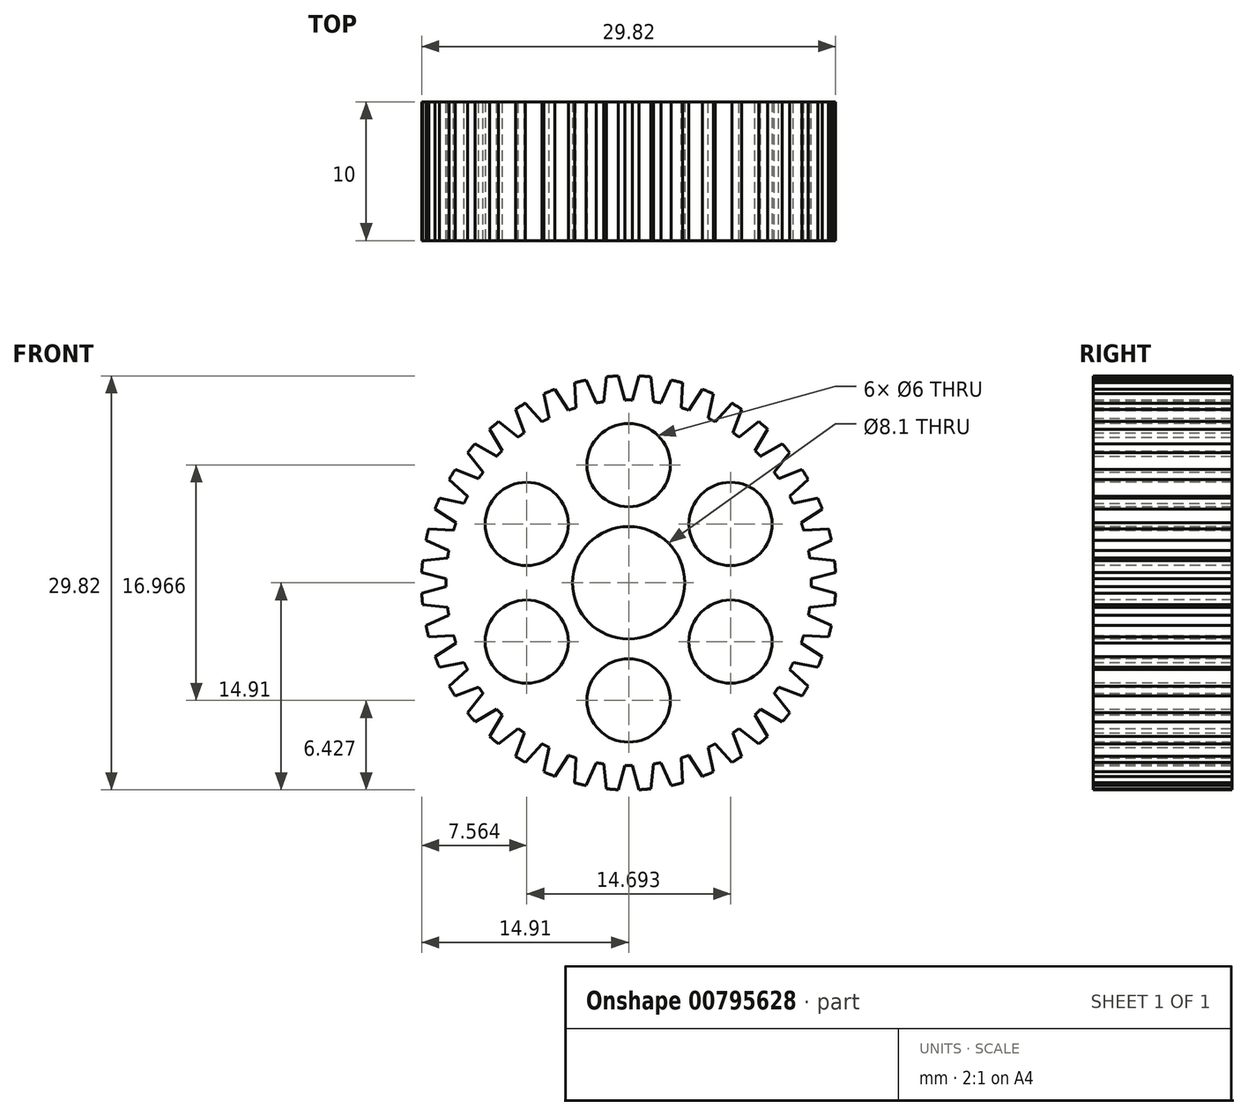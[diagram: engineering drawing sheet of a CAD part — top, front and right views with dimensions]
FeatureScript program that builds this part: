
annotation { "Feature Type Name" : "Feature", "Feature Type Description" : "" }
export const myFeature = defineFeature(function(context is Context, id is Id, definition is map)
    precondition{}
    {
        {
            var Q0;
            Q0=qCreatedBy(makeId("Front.planeOp"),FACE);
            var sketch = newSketch(context, id + "F0", { "sketchPlane" : qUnion([Q0])});
            skLineSegment(sketch, "E0", {"start": v(0, 1.66) * mm, "end": v(0, 25.65) * mm, "construction": true});
            skLineSegment(sketch, "E1", {"start": v(0.28, 20) * mm, "end": v(0.75, 21.74) * mm});
            skLineSegment(sketch, "E2.MirrorCS", {"start": v(-0.28, 20) * mm, "end": v(-0.75, 21.74) * mm});
            skLineSegment(sketch, "E3", {"start": v(-0.28, 20) * mm, "end": v(0, 18.94) * mm, "construction": true});
            skLineSegment(sketch, "E4", {"start": v(0.28, 20) * mm, "end": v(0, 18.94) * mm, "construction": true});
            skLineSegment(sketch, "E5.1.0", {"start": v(-1.78, 19.88) * mm, "end": v(-1.6, 21.67) * mm});
            skLineSegment(sketch, "E5.1.1", {"start": v(-2.34, 19.8) * mm, "end": v(-3.07, 21.44) * mm});
            skLineSegment(sketch, "E5.2.0", {"start": v(-3.8, 19.44) * mm, "end": v(-3.9, 21.24) * mm});
            skLineSegment(sketch, "E5.2.1", {"start": v(-4.34, 19.27) * mm, "end": v(-5.32, 20.78) * mm});
            skLineSegment(sketch, "E5.3.0", {"start": v(-5.73, 18.7) * mm, "end": v(-6.1, 20.45) * mm});
            skLineSegment(sketch, "E5.3.1", {"start": v(-6.23, 18.43) * mm, "end": v(-7.44, 19.77) * mm});
            skLineSegment(sketch, "E5.4.0", {"start": v(-7.51, 17.65) * mm, "end": v(-8.16, 19.33) * mm});
            skLineSegment(sketch, "E5.4.1", {"start": v(-7.97, 17.32) * mm, "end": v(-9.37, 18.45) * mm});
            skLineSegment(sketch, "E5.5.0", {"start": v(-9.11, 16.34) * mm, "end": v(-10.01, 17.9) * mm});
            skLineSegment(sketch, "E5.5.1", {"start": v(-9.51, 15.94) * mm, "end": v(-11.07, 16.84) * mm});
            skLineSegment(sketch, "E5.6.0", {"start": v(-10.49, 14.8) * mm, "end": v(-11.62, 16.2) * mm});
            skLineSegment(sketch, "E5.6.1", {"start": v(-10.82, 14.34) * mm, "end": v(-12.5, 14.99) * mm});
            skLineSegment(sketch, "E5.7.0", {"start": v(-11.6, 13.06) * mm, "end": v(-12.94, 14.27) * mm});
            skLineSegment(sketch, "E5.7.1", {"start": v(-11.86, 12.56) * mm, "end": v(-13.62, 12.93) * mm});
            skLineSegment(sketch, "E5.8.0", {"start": v(-12.44, 11.17) * mm, "end": v(-13.95, 12.15) * mm});
            skLineSegment(sketch, "E5.8.1", {"start": v(-12.61, 10.63) * mm, "end": v(-14.4, 10.72) * mm});
            skLineSegment(sketch, "E5.9.0", {"start": v(-12.96, 9.17) * mm, "end": v(-14.6, 9.9) * mm});
            skLineSegment(sketch, "E5.9.1", {"start": v(-13.05, 8.6) * mm, "end": v(-14.84, 8.42) * mm});
            skLineSegment(sketch, "E5.10.0", {"start": v(-13.17, 7.11) * mm, "end": v(-14.9, 7.58) * mm});
            skLineSegment(sketch, "E5.10.1", {"start": v(-13.17, 6.55) * mm, "end": v(-14.9, 6.08) * mm});
            skLineSegment(sketch, "E5.11.0", {"start": v(-13.05, 5.05) * mm, "end": v(-14.84, 5.24) * mm});
            skLineSegment(sketch, "E5.11.1", {"start": v(-12.96, 4.49) * mm, "end": v(-14.6, 3.76) * mm});
            skLineSegment(sketch, "E5.12.0", {"start": v(-12.61, 3.03) * mm, "end": v(-14.4, 2.94) * mm});
            skLineSegment(sketch, "E5.12.1", {"start": v(-12.44, 2.5) * mm, "end": v(-13.95, 1.51) * mm});
            skLineSegment(sketch, "E5.13.0", {"start": v(-11.86, 1.1) * mm, "end": v(-13.62, 0.73) * mm});
            skLineSegment(sketch, "E5.13.1", {"start": v(-11.6, 0.6) * mm, "end": v(-12.94, -0.6) * mm});
            skLineSegment(sketch, "E5.14.0", {"start": v(-10.82, -0.68) * mm, "end": v(-12.5, -1.33) * mm});
            skLineSegment(sketch, "E5.14.1", {"start": v(-10.49, -1.14) * mm, "end": v(-11.62, -2.54) * mm});
            skLineSegment(sketch, "E5.15.0", {"start": v(-9.51, -2.28) * mm, "end": v(-11.07, -3.18) * mm});
            skLineSegment(sketch, "E5.15.1", {"start": v(-9.11, -2.68) * mm, "end": v(-10.01, -4.24) * mm});
            skLineSegment(sketch, "E5.16.0", {"start": v(-7.97, -3.66) * mm, "end": v(-9.37, -4.79) * mm});
            skLineSegment(sketch, "E5.16.1", {"start": v(-7.51, -3.99) * mm, "end": v(-8.16, -5.67) * mm});
            skLineSegment(sketch, "E5.17.0", {"start": v(-6.23, -4.77) * mm, "end": v(-7.44, -6.11) * mm});
            skLineSegment(sketch, "E5.17.1", {"start": v(-5.73, -5.03) * mm, "end": v(-6.1, -6.8) * mm});
            skLineSegment(sketch, "E5.18.0", {"start": v(-4.34, -5.6) * mm, "end": v(-5.32, -7.12) * mm});
            skLineSegment(sketch, "E5.18.1", {"start": v(-3.8, -5.78) * mm, "end": v(-3.9, -7.58) * mm});
            skLineSegment(sketch, "E5.19.0", {"start": v(-2.34, -6.13) * mm, "end": v(-3.07, -7.78) * mm});
            skLineSegment(sketch, "E5.19.1", {"start": v(-1.78, -6.22) * mm, "end": v(-1.6, -8.01) * mm});
            skLineSegment(sketch, "E5.20.0", {"start": v(-0.28, -6.34) * mm, "end": v(-0.75, -8.08) * mm});
            skLineSegment(sketch, "E5.20.1", {"start": v(0.28, -6.34) * mm, "end": v(0.75, -8.08) * mm});
            skLineSegment(sketch, "E5.21.0", {"start": v(1.78, -6.22) * mm, "end": v(1.6, -8.01) * mm});
            skLineSegment(sketch, "E5.21.1", {"start": v(2.34, -6.13) * mm, "end": v(3.07, -7.78) * mm});
            skLineSegment(sketch, "E5.22.0", {"start": v(3.8, -5.78) * mm, "end": v(3.9, -7.58) * mm});
            skLineSegment(sketch, "E5.22.1", {"start": v(4.34, -5.6) * mm, "end": v(5.32, -7.12) * mm});
            skLineSegment(sketch, "E5.23.0", {"start": v(5.73, -5.03) * mm, "end": v(6.1, -6.8) * mm});
            skLineSegment(sketch, "E5.23.1", {"start": v(6.23, -4.77) * mm, "end": v(7.44, -6.11) * mm});
            skLineSegment(sketch, "E5.24.0", {"start": v(7.51, -3.99) * mm, "end": v(8.16, -5.67) * mm});
            skLineSegment(sketch, "E5.24.1", {"start": v(7.97, -3.66) * mm, "end": v(9.37, -4.79) * mm});
            skLineSegment(sketch, "E5.25.0", {"start": v(9.11, -2.68) * mm, "end": v(10.01, -4.24) * mm});
            skLineSegment(sketch, "E5.25.1", {"start": v(9.51, -2.28) * mm, "end": v(11.07, -3.18) * mm});
            skLineSegment(sketch, "E5.26.0", {"start": v(10.49, -1.14) * mm, "end": v(11.62, -2.54) * mm});
            skLineSegment(sketch, "E5.26.1", {"start": v(10.82, -0.68) * mm, "end": v(12.5, -1.33) * mm});
            skLineSegment(sketch, "E5.27.0", {"start": v(11.6, 0.6) * mm, "end": v(12.94, -0.6) * mm});
            skLineSegment(sketch, "E5.27.1", {"start": v(11.86, 1.1) * mm, "end": v(13.62, 0.73) * mm});
            skLineSegment(sketch, "E5.28.0", {"start": v(12.44, 2.5) * mm, "end": v(13.95, 1.51) * mm});
            skLineSegment(sketch, "E5.28.1", {"start": v(12.61, 3.03) * mm, "end": v(14.4, 2.94) * mm});
            skLineSegment(sketch, "E5.29.0", {"start": v(12.96, 4.49) * mm, "end": v(14.6, 3.76) * mm});
            skLineSegment(sketch, "E5.29.1", {"start": v(13.05, 5.05) * mm, "end": v(14.84, 5.24) * mm});
            skLineSegment(sketch, "E5.30.0", {"start": v(13.17, 6.55) * mm, "end": v(14.9, 6.08) * mm});
            skLineSegment(sketch, "E5.30.1", {"start": v(13.17, 7.11) * mm, "end": v(14.9, 7.58) * mm});
            skLineSegment(sketch, "E5.31.0", {"start": v(13.05, 8.6) * mm, "end": v(14.84, 8.42) * mm});
            skLineSegment(sketch, "E5.31.1", {"start": v(12.96, 9.17) * mm, "end": v(14.6, 9.9) * mm});
            skLineSegment(sketch, "E5.32.0", {"start": v(12.61, 10.63) * mm, "end": v(14.4, 10.72) * mm});
            skLineSegment(sketch, "E5.32.1", {"start": v(12.44, 11.17) * mm, "end": v(13.95, 12.15) * mm});
            skLineSegment(sketch, "E5.33.0", {"start": v(11.86, 12.56) * mm, "end": v(13.62, 12.93) * mm});
            skLineSegment(sketch, "E5.33.1", {"start": v(11.6, 13.06) * mm, "end": v(12.94, 14.27) * mm});
            skLineSegment(sketch, "E5.34.0", {"start": v(10.82, 14.34) * mm, "end": v(12.5, 14.99) * mm});
            skLineSegment(sketch, "E5.34.1", {"start": v(10.49, 14.8) * mm, "end": v(11.62, 16.2) * mm});
            skLineSegment(sketch, "E5.35.0", {"start": v(9.51, 15.94) * mm, "end": v(11.07, 16.84) * mm});
            skLineSegment(sketch, "E5.35.1", {"start": v(9.11, 16.34) * mm, "end": v(10.01, 17.9) * mm});
            skLineSegment(sketch, "E5.36.0", {"start": v(7.97, 17.32) * mm, "end": v(9.37, 18.45) * mm});
            skLineSegment(sketch, "E5.36.1", {"start": v(7.51, 17.65) * mm, "end": v(8.16, 19.33) * mm});
            skLineSegment(sketch, "E5.37.0", {"start": v(6.23, 18.43) * mm, "end": v(7.44, 19.77) * mm});
            skLineSegment(sketch, "E5.37.1", {"start": v(5.73, 18.7) * mm, "end": v(6.1, 20.45) * mm});
            skLineSegment(sketch, "E5.38.0", {"start": v(4.34, 19.27) * mm, "end": v(5.32, 20.78) * mm});
            skLineSegment(sketch, "E5.38.1", {"start": v(3.8, 19.44) * mm, "end": v(3.9, 21.24) * mm});
            skLineSegment(sketch, "E5.39.0", {"start": v(2.34, 19.8) * mm, "end": v(3.07, 21.44) * mm});
            skLineSegment(sketch, "E5.39.1", {"start": v(1.78, 19.88) * mm, "end": v(1.6, 21.67) * mm});
            skPoint(sketch, "E5.center", {"position": v(0, 6.83) * mm});
            skArc(sketch, "E6", {"start": v(0.28, 20) * mm, "mid": v(0, 20) * mm, "end": v(-0.28, 20) * mm});
            skArc(sketch, "E7", {"start": v(-0.75, 21.74) * mm, "mid": v(-1.17, 21.7) * mm, "end": v(-1.6, 21.67) * mm});
            skArc(sketch, "E8.trimOffspring", {"start": v(1.6, 21.67) * mm, "mid": v(1.17, 21.7) * mm, "end": v(0.75, 21.74) * mm});
            skArc(sketch, "E9.trimOffspring", {"start": v(2.34, 19.8) * mm, "mid": v(2.06, 19.84) * mm, "end": v(1.78, 19.88) * mm});
            skArc(sketch, "E10.trimOffspring", {"start": v(3.9, 21.24) * mm, "mid": v(3.48, 21.34) * mm, "end": v(3.07, 21.44) * mm});
            skArc(sketch, "E11.trimOffspring", {"start": v(4.34, 19.27) * mm, "mid": v(4.07, 19.36) * mm, "end": v(3.8, 19.44) * mm});
            skArc(sketch, "E12.trimOffspring", {"start": v(6.1, 20.45) * mm, "mid": v(5.71, 20.62) * mm, "end": v(5.32, 20.78) * mm});
            skArc(sketch, "E13.trimOffspring", {"start": v(6.23, 18.43) * mm, "mid": v(5.98, 18.57) * mm, "end": v(5.73, 18.7) * mm});
            skArc(sketch, "E14.trimOffspring", {"start": v(8.16, 19.33) * mm, "mid": v(7.8, 19.56) * mm, "end": v(7.44, 19.77) * mm});
            skArc(sketch, "E15.trimOffspring", {"start": v(7.97, 17.32) * mm, "mid": v(7.74, 17.49) * mm, "end": v(7.51, 17.65) * mm});
            skArc(sketch, "E16.trimOffspring", {"start": v(10.01, 17.9) * mm, "mid": v(9.7, 18.18) * mm, "end": v(9.37, 18.45) * mm});
            skArc(sketch, "E17.trimOffspring", {"start": v(9.51, 15.94) * mm, "mid": v(9.31, 16.14) * mm, "end": v(9.11, 16.34) * mm});
            skArc(sketch, "E18.trimOffspring", {"start": v(11.62, 16.2) * mm, "mid": v(11.35, 16.52) * mm, "end": v(11.07, 16.84) * mm});
            skArc(sketch, "E19.trimOffspring", {"start": v(10.82, 14.34) * mm, "mid": v(10.66, 14.57) * mm, "end": v(10.49, 14.8) * mm});
            skArc(sketch, "E20.trimOffspring", {"start": v(12.94, 14.27) * mm, "mid": v(12.73, 14.63) * mm, "end": v(12.5, 14.99) * mm});
            skArc(sketch, "E21.trimOffspring", {"start": v(11.86, 12.56) * mm, "mid": v(11.74, 12.8) * mm, "end": v(11.6, 13.06) * mm});
            skArc(sketch, "E22.trimOffspring", {"start": v(13.95, 12.15) * mm, "mid": v(13.79, 12.54) * mm, "end": v(13.62, 12.93) * mm});
            skArc(sketch, "E23.trimOffspring", {"start": v(12.61, 10.63) * mm, "mid": v(12.53, 10.9) * mm, "end": v(12.44, 11.17) * mm});
            skArc(sketch, "E24.trimOffspring", {"start": v(14.6, 9.9) * mm, "mid": v(14.51, 10.31) * mm, "end": v(14.4, 10.72) * mm});
            skArc(sketch, "E25.trimOffspring", {"start": v(13.05, 8.6) * mm, "mid": v(13, 8.9) * mm, "end": v(12.96, 9.17) * mm});
            skArc(sketch, "E26.trimOffspring", {"start": v(14.9, 7.58) * mm, "mid": v(14.88, 8) * mm, "end": v(14.84, 8.42) * mm});
            skArc(sketch, "E27.trimOffspring", {"start": v(14.84, 5.24) * mm, "mid": v(14.88, 5.66) * mm, "end": v(14.9, 6.08) * mm});
            skArc(sketch, "E28.trimOffspring", {"start": v(14.4, 2.94) * mm, "mid": v(14.51, 3.35) * mm, "end": v(14.6, 3.76) * mm});
            skArc(sketch, "E29.trimOffspring", {"start": v(13.62, 0.73) * mm, "mid": v(13.79, 1.12) * mm, "end": v(13.95, 1.51) * mm});
            skArc(sketch, "E30.trimOffspring", {"start": v(12.5, -1.33) * mm, "mid": v(12.73, -0.97) * mm, "end": v(12.94, -0.6) * mm});
            skArc(sketch, "E31.trimOffspring", {"start": v(11.07, -3.18) * mm, "mid": v(11.35, -2.86) * mm, "end": v(11.62, -2.54) * mm});
            skArc(sketch, "E32.trimOffspring", {"start": v(13.17, 6.55) * mm, "mid": v(13.17, 6.83) * mm, "end": v(13.17, 7.11) * mm});
            skArc(sketch, "E33.trimOffspring", {"start": v(12.96, 4.49) * mm, "mid": v(13, 4.77) * mm, "end": v(13.05, 5.05) * mm});
            skArc(sketch, "E34.trimOffspring", {"start": v(12.44, 2.5) * mm, "mid": v(12.53, 2.76) * mm, "end": v(12.61, 3.03) * mm});
            skArc(sketch, "E35.trimOffspring", {"start": v(11.6, 0.6) * mm, "mid": v(11.74, 0.85) * mm, "end": v(11.86, 1.1) * mm});
            skArc(sketch, "E36.trimOffspring", {"start": v(10.49, -1.14) * mm, "mid": v(10.66, -0.91) * mm, "end": v(10.82, -0.68) * mm});
            skArc(sketch, "E37.trimOffspring", {"start": v(9.11, -2.68) * mm, "mid": v(9.31, -2.48) * mm, "end": v(9.51, -2.28) * mm});
            skArc(sketch, "E38.trimOffspring", {"start": v(9.37, -4.79) * mm, "mid": v(9.7, -4.52) * mm, "end": v(10.01, -4.24) * mm});
            skArc(sketch, "E39.trimOffspring", {"start": v(7.44, -6.11) * mm, "mid": v(7.8, -5.9) * mm, "end": v(8.16, -5.67) * mm});
            skArc(sketch, "E40.trimOffspring", {"start": v(5.32, -7.12) * mm, "mid": v(5.71, -6.96) * mm, "end": v(6.1, -6.8) * mm});
            skArc(sketch, "E41.trimOffspring", {"start": v(3.07, -7.78) * mm, "mid": v(3.48, -7.68) * mm, "end": v(3.9, -7.58) * mm});
            skArc(sketch, "E42.trimOffspring", {"start": v(0.75, -8.08) * mm, "mid": v(1.17, -8.05) * mm, "end": v(1.6, -8.01) * mm});
            skArc(sketch, "E43.trimOffspring", {"start": v(-1.6, -8.01) * mm, "mid": v(-1.17, -8.05) * mm, "end": v(-0.75, -8.08) * mm});
            skArc(sketch, "E44.trimOffspring", {"start": v(-3.9, -7.58) * mm, "mid": v(-3.48, -7.68) * mm, "end": v(-3.07, -7.78) * mm});
            skArc(sketch, "E45.trimOffspring", {"start": v(-6.1, -6.8) * mm, "mid": v(-5.71, -6.96) * mm, "end": v(-5.32, -7.12) * mm});
            skArc(sketch, "E46.trimOffspring", {"start": v(-8.16, -5.67) * mm, "mid": v(-7.8, -5.9) * mm, "end": v(-7.44, -6.11) * mm});
            skArc(sketch, "E47.trimOffspring", {"start": v(-6.23, -4.77) * mm, "mid": v(-5.98, -4.9) * mm, "end": v(-5.73, -5.03) * mm});
            skArc(sketch, "E48.trimOffspring", {"start": v(-4.34, -5.6) * mm, "mid": v(-4.07, -5.7) * mm, "end": v(-3.8, -5.78) * mm});
            skArc(sketch, "E49.trimOffspring", {"start": v(-2.34, -6.13) * mm, "mid": v(-2.06, -6.18) * mm, "end": v(-1.78, -6.22) * mm});
            skArc(sketch, "E50.trimOffspring", {"start": v(-0.28, -6.34) * mm, "mid": v(0, -6.34) * mm, "end": v(0.28, -6.34) * mm});
            skArc(sketch, "E51.trimOffspring", {"start": v(1.78, -6.22) * mm, "mid": v(2.06, -6.18) * mm, "end": v(2.34, -6.13) * mm});
            skArc(sketch, "E52.trimOffspring", {"start": v(3.8, -5.78) * mm, "mid": v(4.07, -5.7) * mm, "end": v(4.34, -5.6) * mm});
            skArc(sketch, "E53.trimOffspring", {"start": v(5.73, -5.03) * mm, "mid": v(5.98, -4.9) * mm, "end": v(6.23, -4.77) * mm});
            skArc(sketch, "E54.trimOffspring", {"start": v(7.51, -3.99) * mm, "mid": v(7.74, -3.83) * mm, "end": v(7.97, -3.66) * mm});
            skArc(sketch, "E55.trimOffspring", {"start": v(-10.01, -4.24) * mm, "mid": v(-9.7, -4.52) * mm, "end": v(-9.37, -4.79) * mm});
            skArc(sketch, "E56.trimOffspring", {"start": v(-11.62, -2.54) * mm, "mid": v(-11.35, -2.86) * mm, "end": v(-11.07, -3.18) * mm});
            skArc(sketch, "E57.trimOffspring", {"start": v(-12.94, -0.6) * mm, "mid": v(-12.73, -0.97) * mm, "end": v(-12.5, -1.33) * mm});
            skArc(sketch, "E58.trimOffspring", {"start": v(-13.95, 1.51) * mm, "mid": v(-13.79, 1.12) * mm, "end": v(-13.62, 0.73) * mm});
            skArc(sketch, "E59.trimOffspring", {"start": v(-11.86, 1.1) * mm, "mid": v(-11.74, 0.85) * mm, "end": v(-11.6, 0.6) * mm});
            skArc(sketch, "E60.trimOffspring", {"start": v(-10.82, -0.68) * mm, "mid": v(-10.66, -0.91) * mm, "end": v(-10.49, -1.14) * mm});
            skArc(sketch, "E61.trimOffspring", {"start": v(-9.51, -2.28) * mm, "mid": v(-9.31, -2.48) * mm, "end": v(-9.11, -2.68) * mm});
            skArc(sketch, "E62.trimOffspring", {"start": v(-7.97, -3.66) * mm, "mid": v(-7.74, -3.83) * mm, "end": v(-7.51, -3.99) * mm});
            skArc(sketch, "E63.trimOffspring", {"start": v(-14.6, 3.76) * mm, "mid": v(-14.51, 3.35) * mm, "end": v(-14.4, 2.94) * mm});
            skArc(sketch, "E64.trimOffspring", {"start": v(-14.9, 6.08) * mm, "mid": v(-14.88, 5.66) * mm, "end": v(-14.84, 5.24) * mm});
            skArc(sketch, "E65.trimOffspring", {"start": v(-14.84, 8.42) * mm, "mid": v(-14.88, 8) * mm, "end": v(-14.9, 7.58) * mm});
            skArc(sketch, "E66.trimOffspring", {"start": v(-14.4, 10.72) * mm, "mid": v(-14.51, 10.31) * mm, "end": v(-14.6, 9.9) * mm});
            skArc(sketch, "E67.trimOffspring", {"start": v(-13.62, 12.93) * mm, "mid": v(-13.79, 12.54) * mm, "end": v(-13.95, 12.15) * mm});
            skArc(sketch, "E68.trimOffspring", {"start": v(-12.5, 14.99) * mm, "mid": v(-12.73, 14.63) * mm, "end": v(-12.94, 14.27) * mm});
            skArc(sketch, "E69.trimOffspring", {"start": v(-11.07, 16.84) * mm, "mid": v(-11.35, 16.52) * mm, "end": v(-11.62, 16.2) * mm});
            skArc(sketch, "E70.trimOffspring", {"start": v(-9.37, 18.45) * mm, "mid": v(-9.7, 18.18) * mm, "end": v(-10.01, 17.9) * mm});
            skArc(sketch, "E71.trimOffspring", {"start": v(-7.44, 19.77) * mm, "mid": v(-7.8, 19.56) * mm, "end": v(-8.16, 19.33) * mm});
            skArc(sketch, "E72.trimOffspring", {"start": v(-5.32, 20.78) * mm, "mid": v(-5.71, 20.62) * mm, "end": v(-6.1, 20.45) * mm});
            skArc(sketch, "E73.trimOffspring", {"start": v(-3.07, 21.44) * mm, "mid": v(-3.48, 21.34) * mm, "end": v(-3.9, 21.24) * mm});
            skArc(sketch, "E74.trimOffspring", {"start": v(-1.78, 19.88) * mm, "mid": v(-2.06, 19.84) * mm, "end": v(-2.34, 19.8) * mm});
            skArc(sketch, "E75.trimOffspring", {"start": v(-3.8, 19.44) * mm, "mid": v(-4.07, 19.36) * mm, "end": v(-4.34, 19.27) * mm});
            skArc(sketch, "E76.trimOffspring", {"start": v(-5.73, 18.7) * mm, "mid": v(-5.98, 18.57) * mm, "end": v(-6.23, 18.43) * mm});
            skArc(sketch, "E77.trimOffspring", {"start": v(-7.51, 17.65) * mm, "mid": v(-7.74, 17.49) * mm, "end": v(-7.97, 17.32) * mm});
            skArc(sketch, "E78.trimOffspring", {"start": v(-9.11, 16.34) * mm, "mid": v(-9.31, 16.14) * mm, "end": v(-9.51, 15.94) * mm});
            skArc(sketch, "E79.trimOffspring", {"start": v(-10.49, 14.8) * mm, "mid": v(-10.66, 14.57) * mm, "end": v(-10.82, 14.34) * mm});
            skArc(sketch, "E80.trimOffspring", {"start": v(-11.6, 13.06) * mm, "mid": v(-11.74, 12.8) * mm, "end": v(-11.86, 12.56) * mm});
            skArc(sketch, "E81.trimOffspring", {"start": v(-12.44, 11.17) * mm, "mid": v(-12.53, 10.9) * mm, "end": v(-12.61, 10.63) * mm});
            skArc(sketch, "E82.trimOffspring", {"start": v(-12.96, 9.17) * mm, "mid": v(-13, 8.9) * mm, "end": v(-13.05, 8.6) * mm});
            skArc(sketch, "E83.trimOffspring", {"start": v(-13.17, 7.11) * mm, "mid": v(-13.17, 6.83) * mm, "end": v(-13.17, 6.55) * mm});
            skArc(sketch, "E84.trimOffspring", {"start": v(-13.05, 5.05) * mm, "mid": v(-13, 4.77) * mm, "end": v(-12.96, 4.49) * mm});
            skArc(sketch, "E85.trimOffspring", {"start": v(-12.61, 3.03) * mm, "mid": v(-12.53, 2.76) * mm, "end": v(-12.44, 2.5) * mm});
            skSolve(sketch);
        }
        {
            var Q0;
            Q0 = qSketchRegion(id + "F0", true);
            extrude(context, id + "F1", {"entities" : qUnion([Q0]), "depth" : 10 * mm, "offsetDistance" : 25 * mm});
        }
        {
            var Q0;
            Q0=makeQuery(id+"F1.opExtrude","CAP_FACE",FACE,{"disambiguationData":[OSD([sQuery(id+"F0.wireOp",EDGE,"E1"),sQuery(id+"F0.wireOp",EDGE,"E2.MirrorCS"),sQuery(id+"F0.wireOp",EDGE,"E5.1.0"),sQuery(id+"F0.wireOp",EDGE,"E5.1.1"),sQuery(id+"F0.wireOp",EDGE,"E5.2.0"),sQuery(id+"F0.wireOp",EDGE,"E5.2.1"),sQuery(id+"F0.wireOp",EDGE,"E5.3.0"),sQuery(id+"F0.wireOp",EDGE,"E5.3.1"),sQuery(id+"F0.wireOp",EDGE,"E5.4.0"),sQuery(id+"F0.wireOp",EDGE,"E5.4.1"),sQuery(id+"F0.wireOp",EDGE,"E5.5.0"),sQuery(id+"F0.wireOp",EDGE,"E5.5.1"),sQuery(id+"F0.wireOp",EDGE,"E5.6.0"),sQuery(id+"F0.wireOp",EDGE,"E5.6.1"),sQuery(id+"F0.wireOp",EDGE,"E5.7.0"),sQuery(id+"F0.wireOp",EDGE,"E5.7.1"),sQuery(id+"F0.wireOp",EDGE,"E5.8.0"),sQuery(id+"F0.wireOp",EDGE,"E5.8.1"),sQuery(id+"F0.wireOp",EDGE,"E5.9.0"),sQuery(id+"F0.wireOp",EDGE,"E5.9.1"),sQuery(id+"F0.wireOp",EDGE,"E5.10.0"),sQuery(id+"F0.wireOp",EDGE,"E5.10.1"),sQuery(id+"F0.wireOp",EDGE,"E5.11.0"),sQuery(id+"F0.wireOp",EDGE,"E5.11.1"),sQuery(id+"F0.wireOp",EDGE,"E5.12.0"),sQuery(id+"F0.wireOp",EDGE,"E5.12.1"),sQuery(id+"F0.wireOp",EDGE,"E5.13.0"),sQuery(id+"F0.wireOp",EDGE,"E5.13.1"),sQuery(id+"F0.wireOp",EDGE,"E5.14.0"),sQuery(id+"F0.wireOp",EDGE,"E5.14.1"),sQuery(id+"F0.wireOp",EDGE,"E5.15.0"),sQuery(id+"F0.wireOp",EDGE,"E5.15.1"),sQuery(id+"F0.wireOp",EDGE,"E5.16.0"),sQuery(id+"F0.wireOp",EDGE,"E5.16.1"),sQuery(id+"F0.wireOp",EDGE,"E5.17.0"),sQuery(id+"F0.wireOp",EDGE,"E5.17.1"),sQuery(id+"F0.wireOp",EDGE,"E5.18.0"),sQuery(id+"F0.wireOp",EDGE,"E5.18.1"),sQuery(id+"F0.wireOp",EDGE,"E5.19.0"),sQuery(id+"F0.wireOp",EDGE,"E5.19.1"),sQuery(id+"F0.wireOp",EDGE,"E5.20.0"),sQuery(id+"F0.wireOp",EDGE,"E5.20.1"),sQuery(id+"F0.wireOp",EDGE,"E5.21.0"),sQuery(id+"F0.wireOp",EDGE,"E5.21.1"),sQuery(id+"F0.wireOp",EDGE,"E5.22.0"),sQuery(id+"F0.wireOp",EDGE,"E5.22.1"),sQuery(id+"F0.wireOp",EDGE,"E5.23.0"),sQuery(id+"F0.wireOp",EDGE,"E5.23.1"),sQuery(id+"F0.wireOp",EDGE,"E5.24.0"),sQuery(id+"F0.wireOp",EDGE,"E5.24.1"),sQuery(id+"F0.wireOp",EDGE,"E5.25.0"),sQuery(id+"F0.wireOp",EDGE,"E5.25.1"),sQuery(id+"F0.wireOp",EDGE,"E5.26.0"),sQuery(id+"F0.wireOp",EDGE,"E5.26.1"),sQuery(id+"F0.wireOp",EDGE,"E5.27.0"),sQuery(id+"F0.wireOp",EDGE,"E5.27.1"),sQuery(id+"F0.wireOp",EDGE,"E5.28.0"),sQuery(id+"F0.wireOp",EDGE,"E5.28.1"),sQuery(id+"F0.wireOp",EDGE,"E5.29.0"),sQuery(id+"F0.wireOp",EDGE,"E5.29.1"),sQuery(id+"F0.wireOp",EDGE,"E5.30.0"),sQuery(id+"F0.wireOp",EDGE,"E5.30.1"),sQuery(id+"F0.wireOp",EDGE,"E5.31.0"),sQuery(id+"F0.wireOp",EDGE,"E5.31.1"),sQuery(id+"F0.wireOp",EDGE,"E5.32.0"),sQuery(id+"F0.wireOp",EDGE,"E5.32.1"),sQuery(id+"F0.wireOp",EDGE,"E5.33.0"),sQuery(id+"F0.wireOp",EDGE,"E5.33.1"),sQuery(id+"F0.wireOp",EDGE,"E5.34.0"),sQuery(id+"F0.wireOp",EDGE,"E5.34.1"),sQuery(id+"F0.wireOp",EDGE,"E5.35.0"),sQuery(id+"F0.wireOp",EDGE,"E5.35.1"),sQuery(id+"F0.wireOp",EDGE,"E5.36.0"),sQuery(id+"F0.wireOp",EDGE,"E5.36.1"),sQuery(id+"F0.wireOp",EDGE,"E5.37.0"),sQuery(id+"F0.wireOp",EDGE,"E5.37.1"),sQuery(id+"F0.wireOp",EDGE,"E5.38.0"),sQuery(id+"F0.wireOp",EDGE,"E5.38.1"),sQuery(id+"F0.wireOp",EDGE,"E5.39.0"),sQuery(id+"F0.wireOp",EDGE,"E5.39.1"),sQuery(id+"F0.wireOp",EDGE,"E6"),sQuery(id+"F0.wireOp",EDGE,"E7"),sQuery(id+"F0.wireOp",EDGE,"E8.trimOffspring"),sQuery(id+"F0.wireOp",EDGE,"E9.trimOffspring"),sQuery(id+"F0.wireOp",EDGE,"E10.trimOffspring"),sQuery(id+"F0.wireOp",EDGE,"E11.trimOffspring"),sQuery(id+"F0.wireOp",EDGE,"E12.trimOffspring"),sQuery(id+"F0.wireOp",EDGE,"E13.trimOffspring"),sQuery(id+"F0.wireOp",EDGE,"E14.trimOffspring"),sQuery(id+"F0.wireOp",EDGE,"E15.trimOffspring"),sQuery(id+"F0.wireOp",EDGE,"E16.trimOffspring"),sQuery(id+"F0.wireOp",EDGE,"E17.trimOffspring"),sQuery(id+"F0.wireOp",EDGE,"E18.trimOffspring"),sQuery(id+"F0.wireOp",EDGE,"E19.trimOffspring"),sQuery(id+"F0.wireOp",EDGE,"E20.trimOffspring"),sQuery(id+"F0.wireOp",EDGE,"E21.trimOffspring"),sQuery(id+"F0.wireOp",EDGE,"E22.trimOffspring"),sQuery(id+"F0.wireOp",EDGE,"E23.trimOffspring"),sQuery(id+"F0.wireOp",EDGE,"E24.trimOffspring"),sQuery(id+"F0.wireOp",EDGE,"E25.trimOffspring"),sQuery(id+"F0.wireOp",EDGE,"E26.trimOffspring"),sQuery(id+"F0.wireOp",EDGE,"E27.trimOffspring"),sQuery(id+"F0.wireOp",EDGE,"E28.trimOffspring"),sQuery(id+"F0.wireOp",EDGE,"E29.trimOffspring"),sQuery(id+"F0.wireOp",EDGE,"E30.trimOffspring"),sQuery(id+"F0.wireOp",EDGE,"E31.trimOffspring"),sQuery(id+"F0.wireOp",EDGE,"E32.trimOffspring"),sQuery(id+"F0.wireOp",EDGE,"E33.trimOffspring"),sQuery(id+"F0.wireOp",EDGE,"E34.trimOffspring"),sQuery(id+"F0.wireOp",EDGE,"E35.trimOffspring"),sQuery(id+"F0.wireOp",EDGE,"E36.trimOffspring"),sQuery(id+"F0.wireOp",EDGE,"E37.trimOffspring"),sQuery(id+"F0.wireOp",EDGE,"E38.trimOffspring"),sQuery(id+"F0.wireOp",EDGE,"E39.trimOffspring"),sQuery(id+"F0.wireOp",EDGE,"E40.trimOffspring"),sQuery(id+"F0.wireOp",EDGE,"E41.trimOffspring"),sQuery(id+"F0.wireOp",EDGE,"E42.trimOffspring"),sQuery(id+"F0.wireOp",EDGE,"E43.trimOffspring"),sQuery(id+"F0.wireOp",EDGE,"E44.trimOffspring"),sQuery(id+"F0.wireOp",EDGE,"E45.trimOffspring"),sQuery(id+"F0.wireOp",EDGE,"E46.trimOffspring"),sQuery(id+"F0.wireOp",EDGE,"E47.trimOffspring"),sQuery(id+"F0.wireOp",EDGE,"E48.trimOffspring"),sQuery(id+"F0.wireOp",EDGE,"E49.trimOffspring"),sQuery(id+"F0.wireOp",EDGE,"E50.trimOffspring"),sQuery(id+"F0.wireOp",EDGE,"E51.trimOffspring"),sQuery(id+"F0.wireOp",EDGE,"E52.trimOffspring"),sQuery(id+"F0.wireOp",EDGE,"E53.trimOffspring"),sQuery(id+"F0.wireOp",EDGE,"E54.trimOffspring"),sQuery(id+"F0.wireOp",EDGE,"E55.trimOffspring"),sQuery(id+"F0.wireOp",EDGE,"E56.trimOffspring"),sQuery(id+"F0.wireOp",EDGE,"E57.trimOffspring"),sQuery(id+"F0.wireOp",EDGE,"E58.trimOffspring"),sQuery(id+"F0.wireOp",EDGE,"E59.trimOffspring"),sQuery(id+"F0.wireOp",EDGE,"E60.trimOffspring"),sQuery(id+"F0.wireOp",EDGE,"E61.trimOffspring"),sQuery(id+"F0.wireOp",EDGE,"E62.trimOffspring"),sQuery(id+"F0.wireOp",EDGE,"E63.trimOffspring"),sQuery(id+"F0.wireOp",EDGE,"E64.trimOffspring"),sQuery(id+"F0.wireOp",EDGE,"E65.trimOffspring"),sQuery(id+"F0.wireOp",EDGE,"E66.trimOffspring"),sQuery(id+"F0.wireOp",EDGE,"E67.trimOffspring"),sQuery(id+"F0.wireOp",EDGE,"E68.trimOffspring"),sQuery(id+"F0.wireOp",EDGE,"E69.trimOffspring"),sQuery(id+"F0.wireOp",EDGE,"E70.trimOffspring"),sQuery(id+"F0.wireOp",EDGE,"E71.trimOffspring"),sQuery(id+"F0.wireOp",EDGE,"E72.trimOffspring"),sQuery(id+"F0.wireOp",EDGE,"E73.trimOffspring"),sQuery(id+"F0.wireOp",EDGE,"E74.trimOffspring"),sQuery(id+"F0.wireOp",EDGE,"E75.trimOffspring"),sQuery(id+"F0.wireOp",EDGE,"E76.trimOffspring"),sQuery(id+"F0.wireOp",EDGE,"E77.trimOffspring"),sQuery(id+"F0.wireOp",EDGE,"E78.trimOffspring"),sQuery(id+"F0.wireOp",EDGE,"E79.trimOffspring"),sQuery(id+"F0.wireOp",EDGE,"E80.trimOffspring"),sQuery(id+"F0.wireOp",EDGE,"E81.trimOffspring"),sQuery(id+"F0.wireOp",EDGE,"E82.trimOffspring"),sQuery(id+"F0.wireOp",EDGE,"E83.trimOffspring"),sQuery(id+"F0.wireOp",EDGE,"E84.trimOffspring"),sQuery(id+"F0.wireOp",EDGE,"E85.trimOffspring")])],"isStart":false});
            var sketch = newSketch(context, id + "F2", { "sketchPlane" : qUnion([Q0])});
            skCircle(sketch, "E86", {"center": v(0, 6.83) * mm, "radius": 4.05 * mm});
            skSolve(sketch);
        }
        {
            var Q0;
            Q0 = qSketchRegion(id + "F2", true);
            extrude(context, id + "F3", {"entities" : qUnion([Q0]), "operationType" : NewBodyOperationType.REMOVE, "oppositeDirection" : true, "depth" : 25 * mm, "offsetDistance" : 25 * mm});
        }
        {
            var Q0;
            Q0=makeQuery(id+"F1.opExtrude","CAP_FACE",FACE,{"disambiguationData":[OSD([sQuery(id+"F0.wireOp",EDGE,"E1"),sQuery(id+"F0.wireOp",EDGE,"E2.MirrorCS"),sQuery(id+"F0.wireOp",EDGE,"E5.1.0"),sQuery(id+"F0.wireOp",EDGE,"E5.1.1"),sQuery(id+"F0.wireOp",EDGE,"E5.2.0"),sQuery(id+"F0.wireOp",EDGE,"E5.2.1"),sQuery(id+"F0.wireOp",EDGE,"E5.3.0"),sQuery(id+"F0.wireOp",EDGE,"E5.3.1"),sQuery(id+"F0.wireOp",EDGE,"E5.4.0"),sQuery(id+"F0.wireOp",EDGE,"E5.4.1"),sQuery(id+"F0.wireOp",EDGE,"E5.5.0"),sQuery(id+"F0.wireOp",EDGE,"E5.5.1"),sQuery(id+"F0.wireOp",EDGE,"E5.6.0"),sQuery(id+"F0.wireOp",EDGE,"E5.6.1"),sQuery(id+"F0.wireOp",EDGE,"E5.7.0"),sQuery(id+"F0.wireOp",EDGE,"E5.7.1"),sQuery(id+"F0.wireOp",EDGE,"E5.8.0"),sQuery(id+"F0.wireOp",EDGE,"E5.8.1"),sQuery(id+"F0.wireOp",EDGE,"E5.9.0"),sQuery(id+"F0.wireOp",EDGE,"E5.9.1"),sQuery(id+"F0.wireOp",EDGE,"E5.10.0"),sQuery(id+"F0.wireOp",EDGE,"E5.10.1"),sQuery(id+"F0.wireOp",EDGE,"E5.11.0"),sQuery(id+"F0.wireOp",EDGE,"E5.11.1"),sQuery(id+"F0.wireOp",EDGE,"E5.12.0"),sQuery(id+"F0.wireOp",EDGE,"E5.12.1"),sQuery(id+"F0.wireOp",EDGE,"E5.13.0"),sQuery(id+"F0.wireOp",EDGE,"E5.13.1"),sQuery(id+"F0.wireOp",EDGE,"E5.14.0"),sQuery(id+"F0.wireOp",EDGE,"E5.14.1"),sQuery(id+"F0.wireOp",EDGE,"E5.15.0"),sQuery(id+"F0.wireOp",EDGE,"E5.15.1"),sQuery(id+"F0.wireOp",EDGE,"E5.16.0"),sQuery(id+"F0.wireOp",EDGE,"E5.16.1"),sQuery(id+"F0.wireOp",EDGE,"E5.17.0"),sQuery(id+"F0.wireOp",EDGE,"E5.17.1"),sQuery(id+"F0.wireOp",EDGE,"E5.18.0"),sQuery(id+"F0.wireOp",EDGE,"E5.18.1"),sQuery(id+"F0.wireOp",EDGE,"E5.19.0"),sQuery(id+"F0.wireOp",EDGE,"E5.19.1"),sQuery(id+"F0.wireOp",EDGE,"E5.20.0"),sQuery(id+"F0.wireOp",EDGE,"E5.20.1"),sQuery(id+"F0.wireOp",EDGE,"E5.21.0"),sQuery(id+"F0.wireOp",EDGE,"E5.21.1"),sQuery(id+"F0.wireOp",EDGE,"E5.22.0"),sQuery(id+"F0.wireOp",EDGE,"E5.22.1"),sQuery(id+"F0.wireOp",EDGE,"E5.23.0"),sQuery(id+"F0.wireOp",EDGE,"E5.23.1"),sQuery(id+"F0.wireOp",EDGE,"E5.24.0"),sQuery(id+"F0.wireOp",EDGE,"E5.24.1"),sQuery(id+"F0.wireOp",EDGE,"E5.25.0"),sQuery(id+"F0.wireOp",EDGE,"E5.25.1"),sQuery(id+"F0.wireOp",EDGE,"E5.26.0"),sQuery(id+"F0.wireOp",EDGE,"E5.26.1"),sQuery(id+"F0.wireOp",EDGE,"E5.27.0"),sQuery(id+"F0.wireOp",EDGE,"E5.27.1"),sQuery(id+"F0.wireOp",EDGE,"E5.28.0"),sQuery(id+"F0.wireOp",EDGE,"E5.28.1"),sQuery(id+"F0.wireOp",EDGE,"E5.29.0"),sQuery(id+"F0.wireOp",EDGE,"E5.29.1"),sQuery(id+"F0.wireOp",EDGE,"E5.30.0"),sQuery(id+"F0.wireOp",EDGE,"E5.30.1"),sQuery(id+"F0.wireOp",EDGE,"E5.31.0"),sQuery(id+"F0.wireOp",EDGE,"E5.31.1"),sQuery(id+"F0.wireOp",EDGE,"E5.32.0"),sQuery(id+"F0.wireOp",EDGE,"E5.32.1"),sQuery(id+"F0.wireOp",EDGE,"E5.33.0"),sQuery(id+"F0.wireOp",EDGE,"E5.33.1"),sQuery(id+"F0.wireOp",EDGE,"E5.34.0"),sQuery(id+"F0.wireOp",EDGE,"E5.34.1"),sQuery(id+"F0.wireOp",EDGE,"E5.35.0"),sQuery(id+"F0.wireOp",EDGE,"E5.35.1"),sQuery(id+"F0.wireOp",EDGE,"E5.36.0"),sQuery(id+"F0.wireOp",EDGE,"E5.36.1"),sQuery(id+"F0.wireOp",EDGE,"E5.37.0"),sQuery(id+"F0.wireOp",EDGE,"E5.37.1"),sQuery(id+"F0.wireOp",EDGE,"E5.38.0"),sQuery(id+"F0.wireOp",EDGE,"E5.38.1"),sQuery(id+"F0.wireOp",EDGE,"E5.39.0"),sQuery(id+"F0.wireOp",EDGE,"E5.39.1"),sQuery(id+"F0.wireOp",EDGE,"E6"),sQuery(id+"F0.wireOp",EDGE,"E7"),sQuery(id+"F0.wireOp",EDGE,"E8.trimOffspring"),sQuery(id+"F0.wireOp",EDGE,"E9.trimOffspring"),sQuery(id+"F0.wireOp",EDGE,"E10.trimOffspring"),sQuery(id+"F0.wireOp",EDGE,"E11.trimOffspring"),sQuery(id+"F0.wireOp",EDGE,"E12.trimOffspring"),sQuery(id+"F0.wireOp",EDGE,"E13.trimOffspring"),sQuery(id+"F0.wireOp",EDGE,"E14.trimOffspring"),sQuery(id+"F0.wireOp",EDGE,"E15.trimOffspring"),sQuery(id+"F0.wireOp",EDGE,"E16.trimOffspring"),sQuery(id+"F0.wireOp",EDGE,"E17.trimOffspring"),sQuery(id+"F0.wireOp",EDGE,"E18.trimOffspring"),sQuery(id+"F0.wireOp",EDGE,"E19.trimOffspring"),sQuery(id+"F0.wireOp",EDGE,"E20.trimOffspring"),sQuery(id+"F0.wireOp",EDGE,"E21.trimOffspring"),sQuery(id+"F0.wireOp",EDGE,"E22.trimOffspring"),sQuery(id+"F0.wireOp",EDGE,"E23.trimOffspring"),sQuery(id+"F0.wireOp",EDGE,"E24.trimOffspring"),sQuery(id+"F0.wireOp",EDGE,"E25.trimOffspring"),sQuery(id+"F0.wireOp",EDGE,"E26.trimOffspring"),sQuery(id+"F0.wireOp",EDGE,"E27.trimOffspring"),sQuery(id+"F0.wireOp",EDGE,"E28.trimOffspring"),sQuery(id+"F0.wireOp",EDGE,"E29.trimOffspring"),sQuery(id+"F0.wireOp",EDGE,"E30.trimOffspring"),sQuery(id+"F0.wireOp",EDGE,"E31.trimOffspring"),sQuery(id+"F0.wireOp",EDGE,"E32.trimOffspring"),sQuery(id+"F0.wireOp",EDGE,"E33.trimOffspring"),sQuery(id+"F0.wireOp",EDGE,"E34.trimOffspring"),sQuery(id+"F0.wireOp",EDGE,"E35.trimOffspring"),sQuery(id+"F0.wireOp",EDGE,"E36.trimOffspring"),sQuery(id+"F0.wireOp",EDGE,"E37.trimOffspring"),sQuery(id+"F0.wireOp",EDGE,"E38.trimOffspring"),sQuery(id+"F0.wireOp",EDGE,"E39.trimOffspring"),sQuery(id+"F0.wireOp",EDGE,"E40.trimOffspring"),sQuery(id+"F0.wireOp",EDGE,"E41.trimOffspring"),sQuery(id+"F0.wireOp",EDGE,"E42.trimOffspring"),sQuery(id+"F0.wireOp",EDGE,"E43.trimOffspring"),sQuery(id+"F0.wireOp",EDGE,"E44.trimOffspring"),sQuery(id+"F0.wireOp",EDGE,"E45.trimOffspring"),sQuery(id+"F0.wireOp",EDGE,"E46.trimOffspring"),sQuery(id+"F0.wireOp",EDGE,"E47.trimOffspring"),sQuery(id+"F0.wireOp",EDGE,"E48.trimOffspring"),sQuery(id+"F0.wireOp",EDGE,"E49.trimOffspring"),sQuery(id+"F0.wireOp",EDGE,"E50.trimOffspring"),sQuery(id+"F0.wireOp",EDGE,"E51.trimOffspring"),sQuery(id+"F0.wireOp",EDGE,"E52.trimOffspring"),sQuery(id+"F0.wireOp",EDGE,"E53.trimOffspring"),sQuery(id+"F0.wireOp",EDGE,"E54.trimOffspring"),sQuery(id+"F0.wireOp",EDGE,"E55.trimOffspring"),sQuery(id+"F0.wireOp",EDGE,"E56.trimOffspring"),sQuery(id+"F0.wireOp",EDGE,"E57.trimOffspring"),sQuery(id+"F0.wireOp",EDGE,"E58.trimOffspring"),sQuery(id+"F0.wireOp",EDGE,"E59.trimOffspring"),sQuery(id+"F0.wireOp",EDGE,"E60.trimOffspring"),sQuery(id+"F0.wireOp",EDGE,"E61.trimOffspring"),sQuery(id+"F0.wireOp",EDGE,"E62.trimOffspring"),sQuery(id+"F0.wireOp",EDGE,"E63.trimOffspring"),sQuery(id+"F0.wireOp",EDGE,"E64.trimOffspring"),sQuery(id+"F0.wireOp",EDGE,"E65.trimOffspring"),sQuery(id+"F0.wireOp",EDGE,"E66.trimOffspring"),sQuery(id+"F0.wireOp",EDGE,"E67.trimOffspring"),sQuery(id+"F0.wireOp",EDGE,"E68.trimOffspring"),sQuery(id+"F0.wireOp",EDGE,"E69.trimOffspring"),sQuery(id+"F0.wireOp",EDGE,"E70.trimOffspring"),sQuery(id+"F0.wireOp",EDGE,"E71.trimOffspring"),sQuery(id+"F0.wireOp",EDGE,"E72.trimOffspring"),sQuery(id+"F0.wireOp",EDGE,"E73.trimOffspring"),sQuery(id+"F0.wireOp",EDGE,"E74.trimOffspring"),sQuery(id+"F0.wireOp",EDGE,"E75.trimOffspring"),sQuery(id+"F0.wireOp",EDGE,"E76.trimOffspring"),sQuery(id+"F0.wireOp",EDGE,"E77.trimOffspring"),sQuery(id+"F0.wireOp",EDGE,"E78.trimOffspring"),sQuery(id+"F0.wireOp",EDGE,"E79.trimOffspring"),sQuery(id+"F0.wireOp",EDGE,"E80.trimOffspring"),sQuery(id+"F0.wireOp",EDGE,"E81.trimOffspring"),sQuery(id+"F0.wireOp",EDGE,"E82.trimOffspring"),sQuery(id+"F0.wireOp",EDGE,"E83.trimOffspring"),sQuery(id+"F0.wireOp",EDGE,"E84.trimOffspring"),sQuery(id+"F0.wireOp",EDGE,"E85.trimOffspring")])],"isStart":false});
            var sketch = newSketch(context, id + "F4", { "sketchPlane" : qUnion([Q0])});
            skCircle(sketch, "E87", {"center": v(0, 15.31) * mm, "radius": 3 * mm});
            skCircle(sketch, "E88.1.0", {"center": v(-7.35, 11.07) * mm, "radius": 3 * mm});
            skCircle(sketch, "E88.2.0", {"center": v(-7.35, 2.59) * mm, "radius": 3 * mm});
            skCircle(sketch, "E88.3.0", {"center": v(0, -1.65) * mm, "radius": 3 * mm});
            skCircle(sketch, "E88.4.0", {"center": v(7.35, 2.59) * mm, "radius": 3 * mm});
            skCircle(sketch, "E88.5.0", {"center": v(7.35, 11.07) * mm, "radius": 3 * mm});
            skPoint(sketch, "E88.center", {"position": v(0, 6.83) * mm});
            skSolve(sketch);
        }
        {
            var Q0;
            Q0 = qSketchRegion(id + "F4", true);
            extrude(context, id + "F5", {"entities" : qUnion([Q0]), "operationType" : NewBodyOperationType.REMOVE, "oppositeDirection" : true, "depth" : 25 * mm, "offsetDistance" : 25 * mm});
        }
    });
